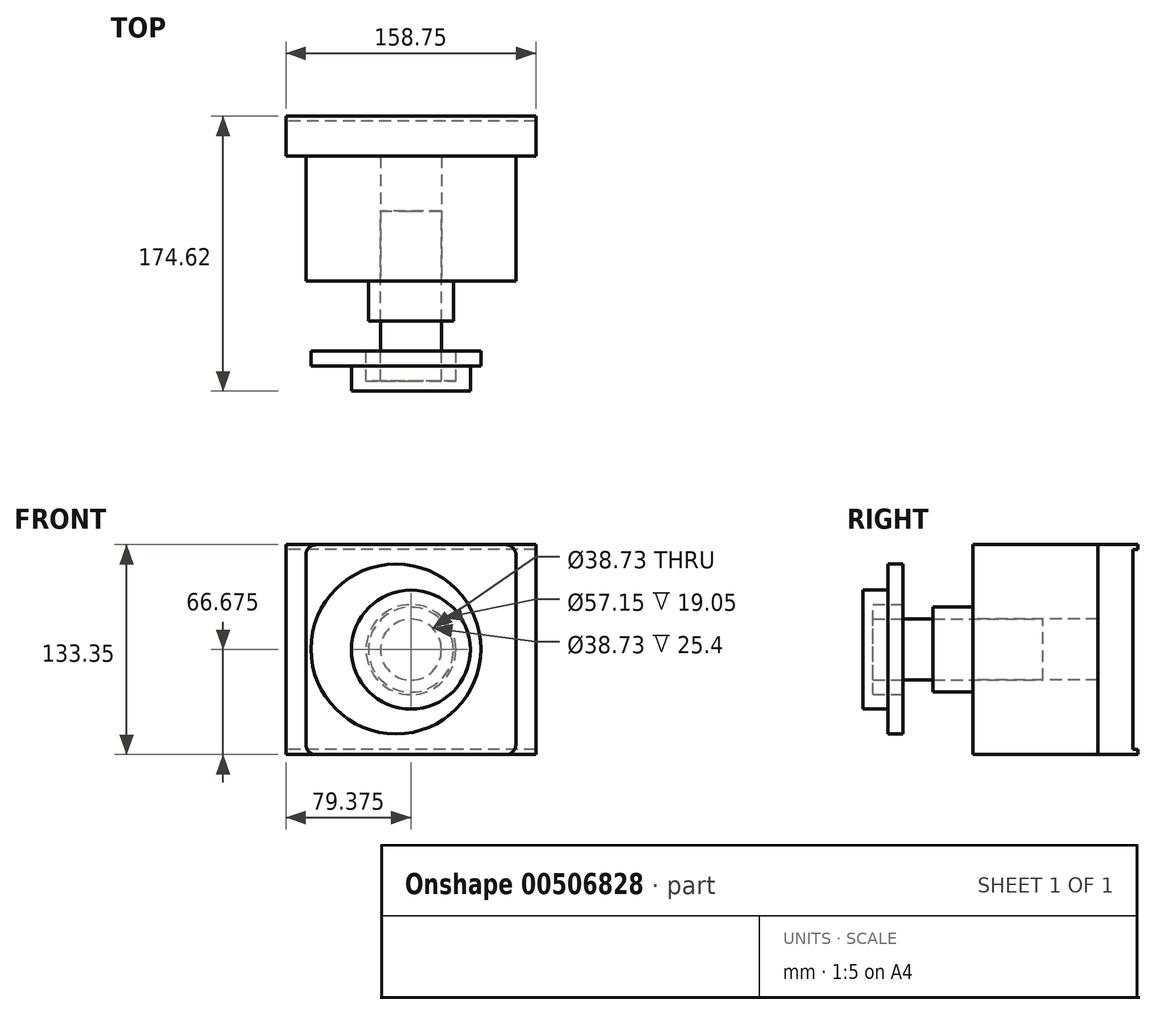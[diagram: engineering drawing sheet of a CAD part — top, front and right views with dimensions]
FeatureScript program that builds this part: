
annotation { "Feature Type Name" : "Feature", "Feature Type Description" : "" }
export const myFeature = defineFeature(function(context is Context, id is Id, definition is map)
    precondition{}
    {
        {
            var Q0;
            Q0=qCreatedBy(makeId("Front.planeOp"),FACE);
            var sketch = newSketch(context, id + "F0", { "sketchPlane" : qUnion([Q0])});
            skLineSegment(sketch, "E0.bottom", {"start": v(-6.35, 0) * mm, "end": v(-127, 0) * mm});
            skLineSegment(sketch, "E0.top", {"start": v(-6.35, 133.35) * mm, "end": v(-127, 133.35) * mm});
            skLineSegment(sketch, "E0.left", {"start": v(0, 6.35) * mm, "end": v(0, 127) * mm});
            skLineSegment(sketch, "E0.right", {"start": v(-133.35, 6.35) * mm, "end": v(-133.35, 127) * mm});
            skPoint(sketch, "E1.visualSharp", {"position": v(-133.35, 133.35) * mm});
            skArc(sketch, "E1.filletArc", {"start": v(-127, 133.35) * mm, "mid": v(-131.5, 131.5) * mm, "end": v(-133.35, 127) * mm});
            skPoint(sketch, "E2.visualSharp", {"position": v(0, 133.35) * mm});
            skArc(sketch, "E2.filletArc", {"start": v(0, 127) * mm, "mid": v(-1.86, 131.5) * mm, "end": v(-6.35, 133.35) * mm});
            skPoint(sketch, "E3.visualSharp", {"position": v(0, 0) * mm});
            skArc(sketch, "E3.filletArc", {"start": v(-6.35, 0) * mm, "mid": v(-1.86, 1.86) * mm, "end": v(0, 6.35) * mm});
            skPoint(sketch, "E4.visualSharp", {"position": v(-133.35, 0) * mm});
            skArc(sketch, "E4.filletArc", {"start": v(-133.35, 6.35) * mm, "mid": v(-131.5, 1.86) * mm, "end": v(-127, 0) * mm});
            skCircle(sketch, "E5", {"center": v(-66.68, 66.67) * mm, "radius": 26.99 * mm});
            skPoint(sketch, "E5.centerSnap0", {"position": v(-66.68, 0) * mm});
            skPoint(sketch, "E5.centerSnap1", {"position": v(-133.35, 66.67) * mm});
            skCircle(sketch, "E6", {"center": v(-66.68, 66.67) * mm, "radius": 19.37 * mm});
            skSolve(sketch);
        }
        {
            var Q0;
            Q0=makeQuery(id+"F0.imprint","IMPRINT",FACE,{"disambiguationData":[TD([[makeQuery(id+"F0.imprint","IMPRINT",EDGE,{"derivedFrom":sQuery(id+"F0.wireOp",EDGE,"E5")}),1.0]])]});
            extrude(context, id + "F1", {"entities" : qUnion([Q0]), "depth" : 25.4 * mm});
        }
        {
            var Q0;
            Q0=makeQuery(id+"F0.imprint","IMPRINT",FACE,{"disambiguationData":[TD([[makeQuery(id+"F0.imprint","IMPRINT",EDGE,{"derivedFrom":sQuery(id+"F0.wireOp",EDGE,"E0.bottom")}),-1.0]])]});
            var Q1;
            Q1=makeQuery(id+"F0.imprint","IMPRINT",FACE,{"disambiguationData":[TD([[makeQuery(id+"F0.imprint","IMPRINT",EDGE,{"derivedFrom":sQuery(id+"F0.wireOp",EDGE,"E5")}),1.0]])]});
            extrude(context, id + "F2", {"entities" : qUnion([Q0, Q1]), "oppositeDirection" : true, "depth" : 79.38 * mm});
        }
        {
            var Q0;
            Q0=makeQuery(id+"F0.imprint","IMPRINT",FACE,{"disambiguationData":[TD([[makeQuery(id+"F0.imprint","IMPRINT",EDGE,{"derivedFrom":sQuery(id+"F0.wireOp",EDGE,"E6")}),1.0]])]});
            extrude(context, id + "F3", {"entities" : qUnion([Q0]), "depth" : 88.9 * mm, "symmetric" : true});
        }
        {
            var Q0;
            Q0=makeQuery(id+"F3.opExtrude","CAP_FACE",FACE,{"disambiguationData":[OSD([sQuery(id+"F0.wireOp",EDGE,"E6")])],"isStart":false});
            var sketch = newSketch(context, id + "F4", { "sketchPlane" : qUnion([Q0])});
            skCircle(sketch, "E7", {"center": v(-66.68, 66.67) * mm, "radius": 28.58 * mm});
            skCircle(sketch, "E8", {"center": v(-76.19, 67.12) * mm, "radius": 53.98 * mm});
            skCircle(sketch, "E9", {"center": v(-66.68, 66.67) * mm, "radius": 37.8 * mm});
            skSolve(sketch);
        }
        {
            var Q0;
            Q0=makeQuery(id+"F4.imprint","IMPRINT",FACE,{"disambiguationData":[TD([[makeQuery(id+"F4.imprint","IMPRINT",EDGE,{"derivedFrom":makeQuery(id+"F3.opExtrude","CAP_EDGE",EDGE,{"disambiguationData":[OSD([sQuery(id+"F0.wireOp",EDGE,"E6")])],"isStart":false})}),1.0]])]});
            var Q1;
            Q1=makeQuery(id+"F4.imprint","IMPRINT",FACE,{"disambiguationData":[TD([[makeQuery(id+"F4.imprint","IMPRINT",EDGE,{"derivedFrom":sQuery(id+"F4.wireOp",EDGE,"E7")}),1.0]])]});
            var Q2;
            Q2=makeQuery(id+"F4.imprint","IMPRINT",FACE,{"disambiguationData":[TD([[makeQuery(id+"F4.imprint","IMPRINT",EDGE,{"derivedFrom":sQuery(id+"F4.wireOp",EDGE,"E7")}),-1.0]])]});
            extrude(context, id + "F5", {"entities" : qUnion([Q0, Q1, Q2]), "depth" : 25.4 * mm});
        }
        {
            var Q0;
            Q0=makeQuery(id+"F4.imprint","IMPRINT",FACE,{"disambiguationData":[TD([[makeQuery(id+"F4.imprint","IMPRINT",EDGE,{"derivedFrom":sQuery(id+"F4.wireOp",EDGE,"E8")}),1.0]])]});
            extrude(context, id + "F6", {"entities" : qUnion([Q0]), "operationType" : NewBodyOperationType.ADD, "depth" : 9.52 * mm});
        }
        {
            var Q0;
            Q0=makeQuery(id+"F4.imprint","IMPRINT",FACE,{"disambiguationData":[TD([[makeQuery(id+"F4.imprint","IMPRINT",EDGE,{"derivedFrom":makeQuery(id+"F3.opExtrude","CAP_EDGE",EDGE,{"disambiguationData":[OSD([sQuery(id+"F0.wireOp",EDGE,"E6")])],"isStart":false})}),1.0]])]});
            var Q1;
            Q1=makeQuery(id+"F4.imprint","IMPRINT",FACE,{"disambiguationData":[TD([[makeQuery(id+"F4.imprint","IMPRINT",EDGE,{"derivedFrom":sQuery(id+"F4.wireOp",EDGE,"E7")}),1.0]])]});
            extrude(context, id + "F7", {"entities" : qUnion([Q0, Q1]), "operationType" : NewBodyOperationType.REMOVE, "depth" : 19.05 * mm});
        }
        {
            var Q0;
            Q0=makeQuery(id+"F4.imprint","IMPRINT",FACE,{"disambiguationData":[TD([[makeQuery(id+"F4.imprint","IMPRINT",EDGE,{"derivedFrom":makeQuery(id+"F3.opExtrude","CAP_EDGE",EDGE,{"disambiguationData":[OSD([sQuery(id+"F0.wireOp",EDGE,"E6")])],"isStart":false})}),1.0]])]});
            extrude(context, id + "F8", {"entities" : qUnion([Q0]), "operationType" : NewBodyOperationType.ADD, "depth" : 19.05 * mm});
        }
        {
            var Q0;
            Q0=makeQuery(id+"F2.opExtrude","CAP_FACE",FACE,{"disambiguationData":[OSD([sQuery(id+"F0.wireOp",EDGE,"E0.bottom"),sQuery(id+"F0.wireOp",EDGE,"E0.top"),sQuery(id+"F0.wireOp",EDGE,"E0.left"),sQuery(id+"F0.wireOp",EDGE,"E0.right"),sQuery(id+"F0.wireOp",EDGE,"E1.filletArc"),sQuery(id+"F0.wireOp",EDGE,"E2.filletArc"),sQuery(id+"F0.wireOp",EDGE,"E3.filletArc"),sQuery(id+"F0.wireOp",EDGE,"E4.filletArc"),sQuery(id+"F0.wireOp",EDGE,"E6")])],"isStart":false});
            var sketch = newSketch(context, id + "F9", { "sketchPlane" : qUnion([Q0])});
            skLineSegment(sketch, "E10.bottom", {"start": v(-12.7, 133.35) * mm, "end": v(146.05, 133.35) * mm});
            skLineSegment(sketch, "E10.top", {"start": v(-12.7, 0) * mm, "end": v(146.05, 0) * mm});
            skLineSegment(sketch, "E10.left", {"start": v(-12.7, 133.35) * mm, "end": v(-12.7, 0) * mm});
            skLineSegment(sketch, "E10.right", {"start": v(146.05, 133.35) * mm, "end": v(146.05, 0) * mm});
            skSolve(sketch);
        }
        {
            var Q0;
            {var subQ0=sQuery(id+"F9.wireOp",EDGE,"E10.left");Q0=makeQuery(id+"F9.imprint","IMPRINT",FACE,{"disambiguationData":[TD([[makeQuery(id+"F9.imprint","IMPRINT",EDGE,{"derivedFrom":subQ0}),1.0]])]});}
            var Q1;
            Q1=makeQuery(id+"F9.imprint","IMPRINT",FACE,{"disambiguationData":[TD([[makeQuery(id+"F9.imprint","IMPRINT",EDGE,{"derivedFrom":makeQuery(id+"F2.opExtrude","CAP_EDGE",EDGE,{"disambiguationData":[OSD([sQuery(id+"F0.wireOp",EDGE,"E0.left")])],"isStart":false})}),-1.0]])]});
            var Q2;
            {var subQ2=sQuery(id+"F9.wireOp",EDGE,"E10.right");Q2=makeQuery(id+"F9.imprint","IMPRINT",FACE,{"disambiguationData":[TD([[makeQuery(id+"F9.imprint","IMPRINT",EDGE,{"derivedFrom":subQ2}),-1.0]])]});}
            var Q3;
            Q3=makeQuery(id+"F9.imprint","IMPRINT",FACE,{"disambiguationData":[TD([[makeQuery(id+"F9.imprint","IMPRINT",EDGE,{"derivedFrom":makeQuery(id+"F2.opExtrude","CAP_EDGE",EDGE,{"disambiguationData":[OSD([sQuery(id+"F0.wireOp",EDGE,"E6")])],"isStart":false})}),-1.0]])]});
            extrude(context, id + "F10", {"entities" : qUnion([Q0, Q1, Q2, Q3]), "depth" : 22.22 * mm});
        }
        {
            var Q0;
            Q0=makeQuery(id+"F10.opExtrude","SWEPT_FACE",FACE,{"disambiguationData":[OSD([sQuery(id+"F9.wireOp",EDGE,"E10.right")])]});
            var sketch = newSketch(context, id + "F11", { "sketchPlane" : qUnion([Q0])});
            skLineSegment(sketch, "E11", {"start": v(-101.6, 133.35) * mm, "end": v(-101.6, 0) * mm});
            skLineSegment(sketch, "E12", {"start": v(-101.6, 133.35) * mm, "end": v(-104.77, 133.35) * mm});
            skLineSegment(sketch, "E13", {"start": v(-104.77, 133.35) * mm, "end": v(-104.77, 130.17) * mm});
            skLineSegment(sketch, "E14", {"start": v(-104.77, 130.17) * mm, "end": v(-101.6, 130.17) * mm});
            skLineSegment(sketch, "E15", {"start": v(-101.6, 0) * mm, "end": v(-104.77, 0) * mm});
            skLineSegment(sketch, "E16", {"start": v(-104.77, 0) * mm, "end": v(-104.77, 3.18) * mm});
            skLineSegment(sketch, "E17", {"start": v(-104.77, 3.18) * mm, "end": v(-101.6, 3.18) * mm});
            skSolve(sketch);
        }
        {
            var Q0;
            {var subQ0=sQuery(id+"F11.wireOp",EDGE,"E12");Q0=makeQuery(id+"F11.imprint","IMPRINT",FACE,{"disambiguationData":[TD([[makeQuery(id+"F11.imprint","IMPRINT",EDGE,{"derivedFrom":subQ0}),1.0]])]});}
            var Q1;
            {var subQ0=sQuery(id+"F11.wireOp",EDGE,"E15");Q1=makeQuery(id+"F11.imprint","IMPRINT",FACE,{"disambiguationData":[TD([[makeQuery(id+"F11.imprint","IMPRINT",EDGE,{"derivedFrom":subQ0}),-1.0]])]});}
            extrude(context, id + "F12", {"entities" : qUnion([Q0, Q1]), "operationType" : NewBodyOperationType.ADD, "oppositeDirection" : true, "depth" : 158.75 * mm});
        }
    });
